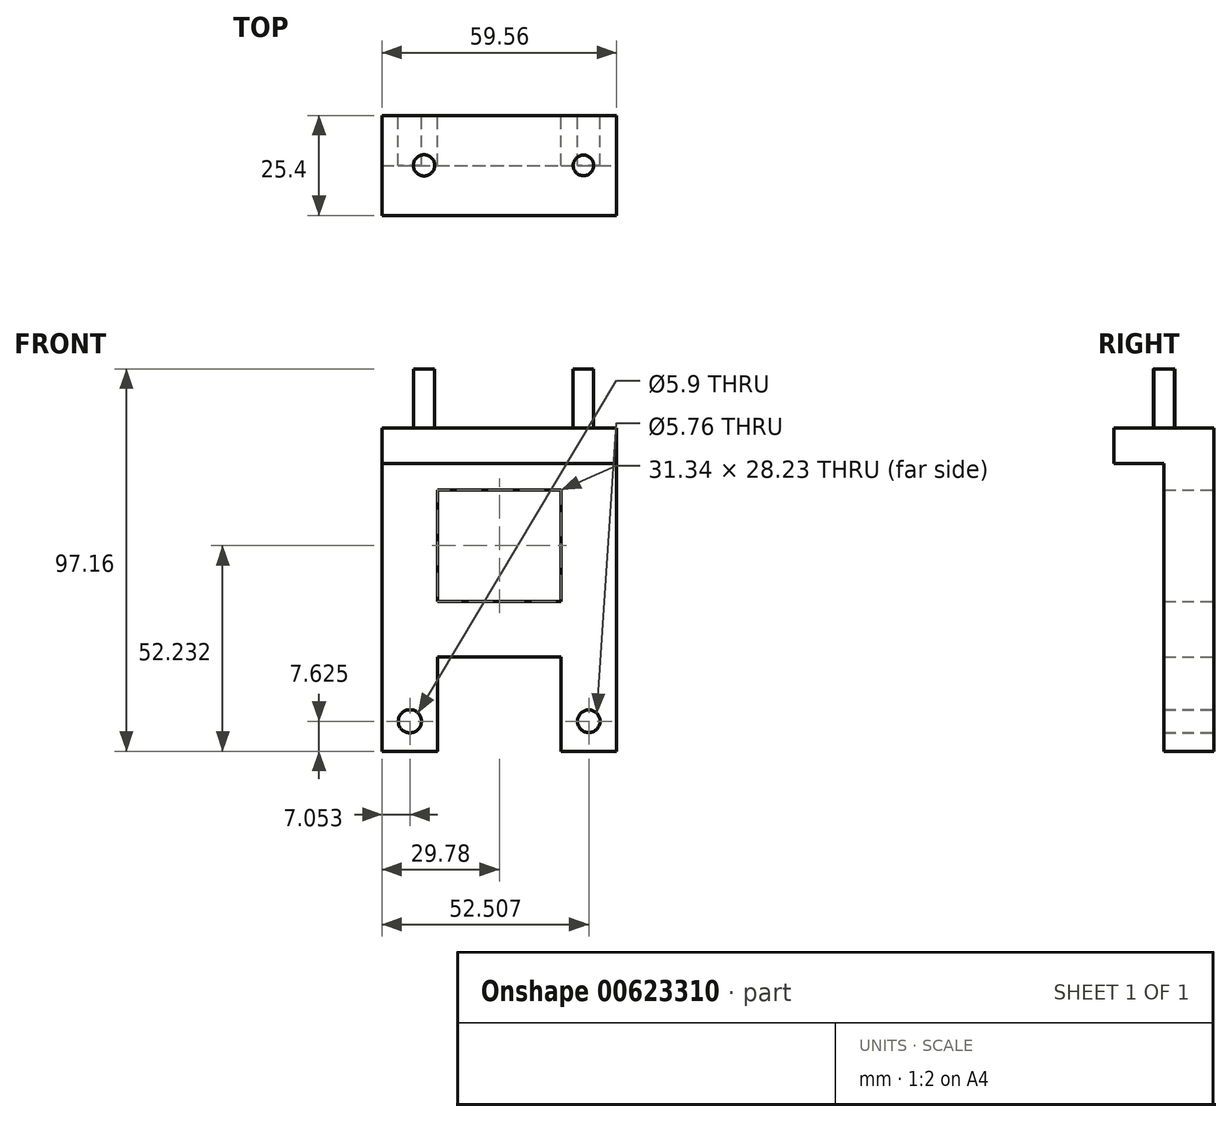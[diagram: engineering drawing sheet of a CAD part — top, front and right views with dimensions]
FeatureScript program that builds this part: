
annotation { "Feature Type Name" : "Feature", "Feature Type Description" : "" }
export const myFeature = defineFeature(function(context is Context, id is Id, definition is map)
    precondition{}
    {
        {
            var Q0;
            Q0=qCreatedBy(makeId("Front.planeOp"),FACE);
            var sketch = newSketch(context, id + "F0", { "sketchPlane" : qUnion([Q0])});
            skLineSegment(sketch, "E0.bottom", {"start": v(-29.78, 41.08) * mm, "end": v(29.78, 41.08) * mm});
            skLineSegment(sketch, "E0.top", {"start": v(-29.78, -41.08) * mm, "end": v(-15.67, -41.08) * mm});
            skLineSegment(sketch, "E0.left", {"start": v(-29.78, 41.08) * mm, "end": v(-29.78, -41.08) * mm});
            skLineSegment(sketch, "E0.right", {"start": v(29.78, 41.08) * mm, "end": v(29.78, -41.08) * mm});
            skPoint(sketch, "E0.middle", {"position": v(0, 0) * mm});
            skLineSegment(sketch, "E1", {"start": v(-29.78, 32.04) * mm, "end": v(29.78, 32.04) * mm});
            skLineSegment(sketch, "E2.bottom", {"start": v(-15.67, -17.08) * mm, "end": v(15.67, -17.08) * mm});
            skLineSegment(sketch, "E2.left", {"start": v(-15.67, -17.08) * mm, "end": v(-15.67, -41.08) * mm});
            skLineSegment(sketch, "E2.right", {"start": v(15.67, -17.08) * mm, "end": v(15.67, -41.08) * mm});
            skPoint(sketch, "E2.middle", {"position": v(0, -41.08) * mm});
            skPoint(sketch, "E3.orphan", {"position": v(-15.67, -65.07) * mm});
            skPoint(sketch, "E4.orphan", {"position": v(15.67, -65.07) * mm});
            skLineSegment(sketch, "E5.trimOffspring", {"start": v(15.67, -41.08) * mm, "end": v(29.78, -41.08) * mm});
            skLineSegment(sketch, "E6.bottom", {"start": v(-15.67, 25.27) * mm, "end": v(15.67, 25.27) * mm});
            skLineSegment(sketch, "E6.top", {"start": v(-15.67, -2.96) * mm, "end": v(15.67, -2.96) * mm});
            skLineSegment(sketch, "E6.left", {"start": v(-15.67, 25.27) * mm, "end": v(-15.67, -2.96) * mm});
            skLineSegment(sketch, "E6.right", {"start": v(15.67, 25.27) * mm, "end": v(15.67, -2.96) * mm});
            skCircle(sketch, "E7", {"center": v(-22.73, -33.45) * mm, "radius": 2.95 * mm});
            skPoint(sketch, "E7.centerSnap0", {"position": v(-22.73, -41.08) * mm});
            skCircle(sketch, "E8", {"center": v(22.73, -33.45) * mm, "radius": 2.88 * mm});
            skPoint(sketch, "E8.centerSnap0", {"position": v(22.73, -41.08) * mm});
            skSolve(sketch);
        }
        {
            var Q0;
            {var subQ1=sQuery(id+"F0.wireOp",EDGE,"E0.top");Q0=makeQuery(id+"F0.imprint","IMPRINT",FACE,{"disambiguationData":[TD([[makeQuery(id+"F0.imprint","IMPRINT",EDGE,{"derivedFrom":subQ1}),1.0]])]});}
            extrude(context, id + "F1", {"entities" : qUnion([Q0]), "depth" : 12.7 * mm, "offsetDistance" : 25.4 * mm});
        }
        {
            var Q0;
            {var subQ0=sQuery(id+"F0.wireOp",EDGE,"E0.bottom");Q0=makeQuery(id+"F0.imprint","IMPRINT",FACE,{"disambiguationData":[TD([[makeQuery(id+"F0.imprint","IMPRINT",EDGE,{"derivedFrom":subQ0}),-1.0]])]});}
            extrude(context, id + "F2", {"entities" : qUnion([Q0]), "operationType" : NewBodyOperationType.ADD, "depth" : 25.4 * mm, "offsetDistance" : 25.4 * mm});
        }
        {
            var Q0;
            Q0=makeQuery(id+"F2.opExtrude","SWEPT_FACE",FACE,{"disambiguationData":[OSD([sQuery(id+"F0.wireOp",EDGE,"E0.bottom")])]});
            var sketch = newSketch(context, id + "F3", { "sketchPlane" : qUnion([Q0])});
            skPoint(sketch, "E9.centerSnap0", {"position": v(-29.78, -12.7) * mm});
            skCircle(sketch, "E10", {"center": v(-19.12, -12.7) * mm, "radius": 2.7 * mm});
            skCircle(sketch, "E11", {"center": v(21.37, -12.7) * mm, "radius": 2.61 * mm});
            skPoint(sketch, "E11.centerSnap0", {"position": v(29.78, -12.7) * mm});
            skSolve(sketch);
        }
        {
            var Q0;
            Q0=makeQuery(id+"F3.imprint","IMPRINT",FACE,{"disambiguationData":[TD([[makeQuery(id+"F3.imprint","IMPRINT",EDGE,{"derivedFrom":sQuery(id+"F3.wireOp",EDGE,"E10")}),1.0]])]});
            extrude(context, id + "F4", {"entities" : qUnion([Q0]), "operationType" : NewBodyOperationType.ADD, "depth" : 15 * mm, "offsetDistance" : 25 * mm});
        }
        {
            var Q0;
            Q0=makeQuery(id+"F3.imprint","IMPRINT",FACE,{"disambiguationData":[TD([[makeQuery(id+"F3.imprint","IMPRINT",EDGE,{"derivedFrom":sQuery(id+"F3.wireOp",EDGE,"E11")}),1.0]])]});
            extrude(context, id + "F5", {"entities" : qUnion([Q0]), "operationType" : NewBodyOperationType.ADD, "depth" : 15 * mm, "offsetDistance" : 25 * mm});
        }
    });
